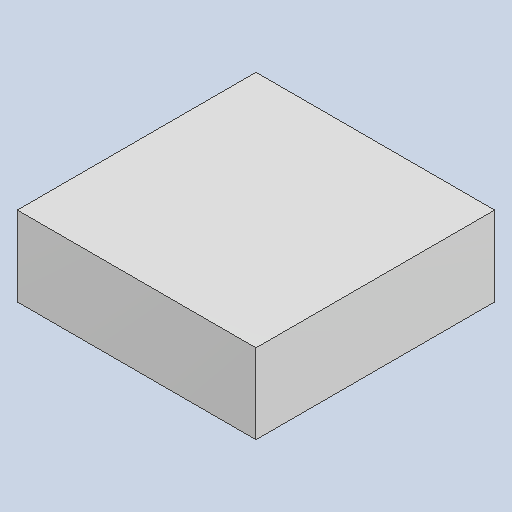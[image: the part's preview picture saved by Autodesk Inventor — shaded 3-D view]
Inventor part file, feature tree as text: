
AUTODESK INVENTOR PART (.ipt)
format: ipt  version: 2023.4 (Build 274418000, 418)  size: 79,872 bytes
history: native  units: mm
features: extrude x1
ambient origin geometry x8: Origin, YZ Plane, XZ Plane, XY Plane, X Axis, Y Axis, Z Axis, Center Point
bodies: Solid1 (feature_tree)
feature tree (1):
  extrude  "Extruded_13"  [1 undecoded]
note: 1 required parameter value undecoded (feature->parameter linkage not recoverable at this tier; creation-order binding heuristic only, values carry confidence <= 0.55)
